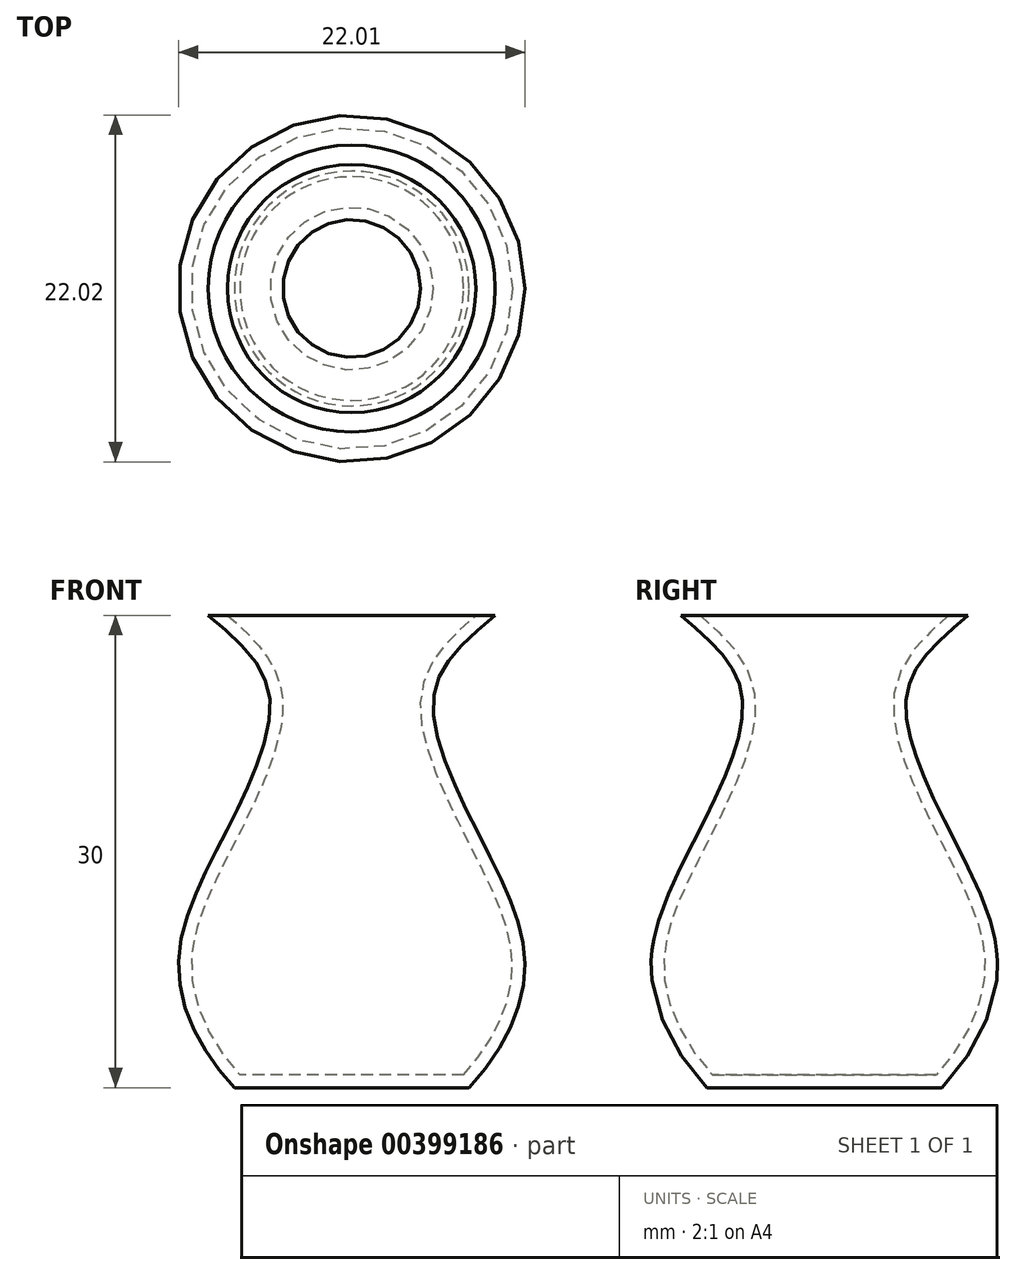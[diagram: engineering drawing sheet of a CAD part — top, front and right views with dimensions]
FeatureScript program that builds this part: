
annotation { "Feature Type Name" : "Feature", "Feature Type Description" : "" }
export const myFeature = defineFeature(function(context is Context, id is Id, definition is map)
    precondition{}
    {
        {
            var Q0;
            Q0=qCreatedBy(makeId("Front.planeOp"),FACE);
            var sketch = newSketch(context, id + "F0", { "sketchPlane" : qUnion([Q0])});
            skFitSpline(sketch, "E0", {"points": [v(7.46, 0) * mm, v(11, 7.63) * mm, v(8.32, 15.6) * mm, v(5.2, 24.8) * mm, v(9.11, 30) * mm], "startDerivative": vector(26, 27.66) * mm, "endDerivative": vector(26.94, 22.97) * mm});
            skLineSegment(sketch, "E1", {"start": v(0, 0) * mm, "end": v(7.46, 0) * mm});
            skLineSegment(sketch, "E2", {"start": v(9.11, 30) * mm, "end": v(0, 30) * mm});
            skLineSegment(sketch, "E3", {"start": v(0, 30) * mm, "end": v(0, 0) * mm});
            skLineSegment(sketch, "E4", {"start": v(0, 36.63) * mm, "end": v(0, -9.17) * mm, "construction": true});
            skSolve(sketch);
        }
        {
            var Q0;
            Q0=makeQuery(id+"F0.imprint","IMPRINT",FACE,{"disambiguationData":[TD([[makeQuery(id+"F0.imprint","IMPRINT",EDGE,{"derivedFrom":sQuery(id+"F0.wireOp",EDGE,"E0")}),1.0]])]});
            var Q1;
            Q1=sQuery(id+"F0.wireOp",EDGE,"E4");
            revolve(context, id + "F1", {"entities" : qUnion([Q0]), "axis" : qUnion([Q1]), "revolveType" : RevolveType.FULL});
        }
        {
            var Q0;
            Q0=makeQuery(id+"F1.opRevolve","SWEPT_FACE",FACE,{"disambiguationData":[OSD([sQuery(id+"F0.wireOp",EDGE,"E2")])]});
            shell(context, id + "F2", {"entities" : qUnion([Q0]), "thickness" : 0.8 * mm});
        }
    });
